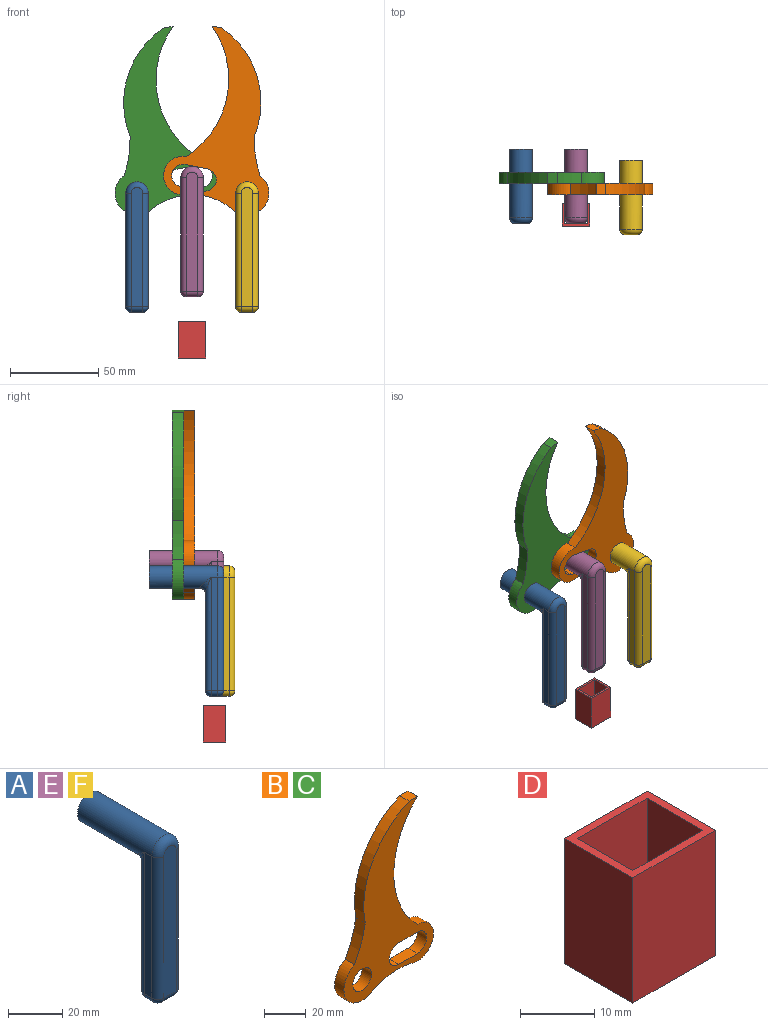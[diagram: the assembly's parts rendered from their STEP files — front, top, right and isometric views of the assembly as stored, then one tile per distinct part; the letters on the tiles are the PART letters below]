
ASSEMBLY  parts=6 mates=5
PART A: 23 faces, bbox 13.7x42x74.2 mm
  f0: cylinder r=6.35mm len=38.86mm, axis (0,1,0), area 1383.6mm2, adj f1,f3,f5,f7,f8,f10,f20
  f1: plane 12.7x12.7mm, normal (0,1,0), area 126.7mm2, adj f0
  f2: plane 55.23x6.42mm, normal (0,1,0), area 352.4mm2, adj f8,f9,f12,f13
  f3: plane 64.16x3.92mm, normal (-1,0,0), area 251.7mm2, adj f0,f9,f14,f17
  f4: plane 6.42x3.92mm, normal (0,0,-1), area 25.2mm2, adj f13,f14,f18,f19
  f5: plane 64.16x3.92mm, normal (1,0,0), area 251.7mm2, adj f0,f12,f18,f22
  f6: plane 67.37x6.42mm, normal (0,-1,0), area 428.3mm2, adj f17,f19,f20,f22
  f7: bspline ~9.27x6.28mm, area 23.8mm2, adj f0,f8,f9
  f8: torus R=9.49mm, axis (0,-1,0), area 25.5mm2, adj f0,f2,f7,f10
  f9: cylinder r=3.14mm len=64.16mm, axis (0,0,-1), area 290.6mm2, adj f2,f3,f7,f11
  f10: bspline ~9.27x6.28mm, area 23.8mm2, adj f0,f8,f12
  f11: sphere r=3.14mm, area 15.5mm2, adj f9,f13,f14
  f12: cylinder r=3.14mm len=64.16mm, axis (0,0,1), area 290.6mm2, adj f2,f5,f10,f15
  f13: cylinder r=3.14mm len=6.42mm, axis (1,0,0), area 31.7mm2, adj f2,f4,f11,f15
  f14: cylinder r=3.14mm len=3.92mm, axis (0,-1,0), area 19.3mm2, adj f3,f4,f11,f16
  f15: sphere r=3.14mm, area 15.5mm2, adj f12,f13,f18
  f16: sphere r=3.14mm, area 15.5mm2, adj f14,f17,f19
  f17: cylinder r=3.14mm len=64.16mm, axis (0,0,1), area 316.3mm2, adj f3,f6,f16,f20
  f18: cylinder r=3.14mm len=3.92mm, axis (0,1,0), area 19.3mm2, adj f4,f5,f15,f21
  f19: cylinder r=3.14mm len=6.42mm, axis (-1,0,0), area 31.7mm2, adj f4,f6,f16,f21
  f20: torus R=3.21mm, axis (0,-1,0), area 80.7mm2, adj f0,f6,f17,f22
  f21: sphere r=3.14mm, area 15.5mm2, adj f18,f19,f22
  f22: cylinder r=3.14mm len=64.16mm, axis (0,0,-1), area 316.3mm2, adj f5,f6,f20,f21
PART B: 14 faces, bbox 60.8x6.4x101.4 mm
  f0: cylinder r=52.31mm len=75.18mm, axis (0,1,0), area 532.7mm2, adj f1,f9,f12,f13
  f1: plane 6.35x5.57mm, normal (0,0,1), area 35.4mm2, adj f0,f2,f12,f13
  f2: cylinder r=51mm len=56.78mm, axis (0,1,0), area 440.3mm2, adj f1,f3,f12,f13
  f3: cylinder r=63.81mm len=20.92mm, axis (0,1,0), area 141.4mm2, adj f2,f4,f12,f13
  f4: cylinder r=12.4mm len=23.65mm, axis (0,1,0), area 260.3mm2, adj f3,f5,f12,f13
  f5: cylinder r=36.77mm len=25.93mm, axis (0,1,0), area 169.6mm2, adj f4,f9,f12,f13
  f6: cylinder r=6.35mm len=12.7mm, axis (0,1,0), area 126.7mm2, adj f7,f10,f12,f13
  f7: plane 12.7x6.35mm, normal (0,0,1), area 80.6mm2, adj f6,f8,f12,f13
  f8: cylinder r=6.35mm len=12.7mm, axis (0,1,0), area 126.7mm2, adj f7,f10,f12,f13
  f9: cylinder r=10.94mm len=21.88mm, axis (0,1,0), area 247.8mm2, adj f0,f5,f12,f13
  f10: plane 12.7x6.35mm, normal (0,0,-1), area 80.6mm2, adj f6,f8,f12,f13
  f11: cylinder r=6.35mm len=12.7mm, axis (0,1,0), area 253.4mm2, adj f12,f13
  f12: plane 101.35x60.77mm, normal (0,-1,0), area 2365.1mm2, adj f0,f1,f2,f3,f4,f5,f6,f7
  f13: plane 101.35x60.77mm, normal (0,1,0), area 2365.1mm2, adj f0,f1,f2,f3,f4,f5,f6,f7
PART C: same geometry as B
PART D: 10 faces, bbox 15.6x13x20.6 mm
  f0: plane 20.6x13.24mm, normal (0,1,0), area 272.7mm2, adj f1,f7,f8,f9
  f1: plane 20.6x10.55mm, normal (-1,0,0), area 217.4mm2, adj f0,f2,f8,f9
  f2: plane 20.6x13.24mm, normal (0,-1,0), area 272.7mm2, adj f1,f7,f8,f9
  f3: plane 20.6x15.64mm, normal (0,-1,0), area 322.1mm2, adj f4,f6,f8,f9
  f4: plane 20.6x12.95mm, normal (-1,0,0), area 266.8mm2, adj f3,f5,f8,f9
  f5: plane 20.6x15.64mm, normal (0,1,0), area 322.1mm2, adj f4,f6,f8,f9
  f6: plane 20.6x12.95mm, normal (1,0,0), area 266.8mm2, adj f3,f5,f8,f9
  f7: plane 20.6x10.55mm, normal (1,0,0), area 217.4mm2, adj f0,f2,f8,f9
  f8: plane 15.64x12.95mm, normal (0,0,1), area 62.9mm2, adj f0,f1,f2,f3,f4,f5,f6,f7
  f9: plane 15.64x12.95mm, normal (0,0,-1), area 62.9mm2, adj f0,f1,f2,f3,f4,f5,f6,f7
PART E: same geometry as A
PART F: same geometry as A
PLACE A t=(-86.54,-46.25,27.02)mm fixed
PLACE B rot(axis=(-0.1,0,-1),180deg) t=(-60.59,-72.03,36.94)mm
PLACE C rot(axis=(0,-1,0),10.6deg) t=(-50.28,-59.33,36.7)mm
PLACE D t=(-55.46,-46.25,1.15)mm fixed
PLACE E t=(-55.46,-46.25,35.73)mm
PLACE F t=(-24.39,-52.6,27.02)mm fixed
MATE pin_slot B.f12 <-> E.f0  axis (0,1,0) through (-54.35,-65.68,35.73)mm
MATE slider D.f8 <-> E.f4  axis (0,0,1) through (-55.46,-83.15,-45.55)mm
MATE revolute B.f4 <-> F.f0  axis (0,-1,0) through (-24.39,-72.03,27.02)mm
MATE revolute C.f4 <-> A.f0  axis (0,-1,0) through (-86.54,-65.68,27.02)mm
MATE pin_slot E.f0 <-> C.f12  axis (0,1,0) through (-55.46,-65.68,35.73)mm
